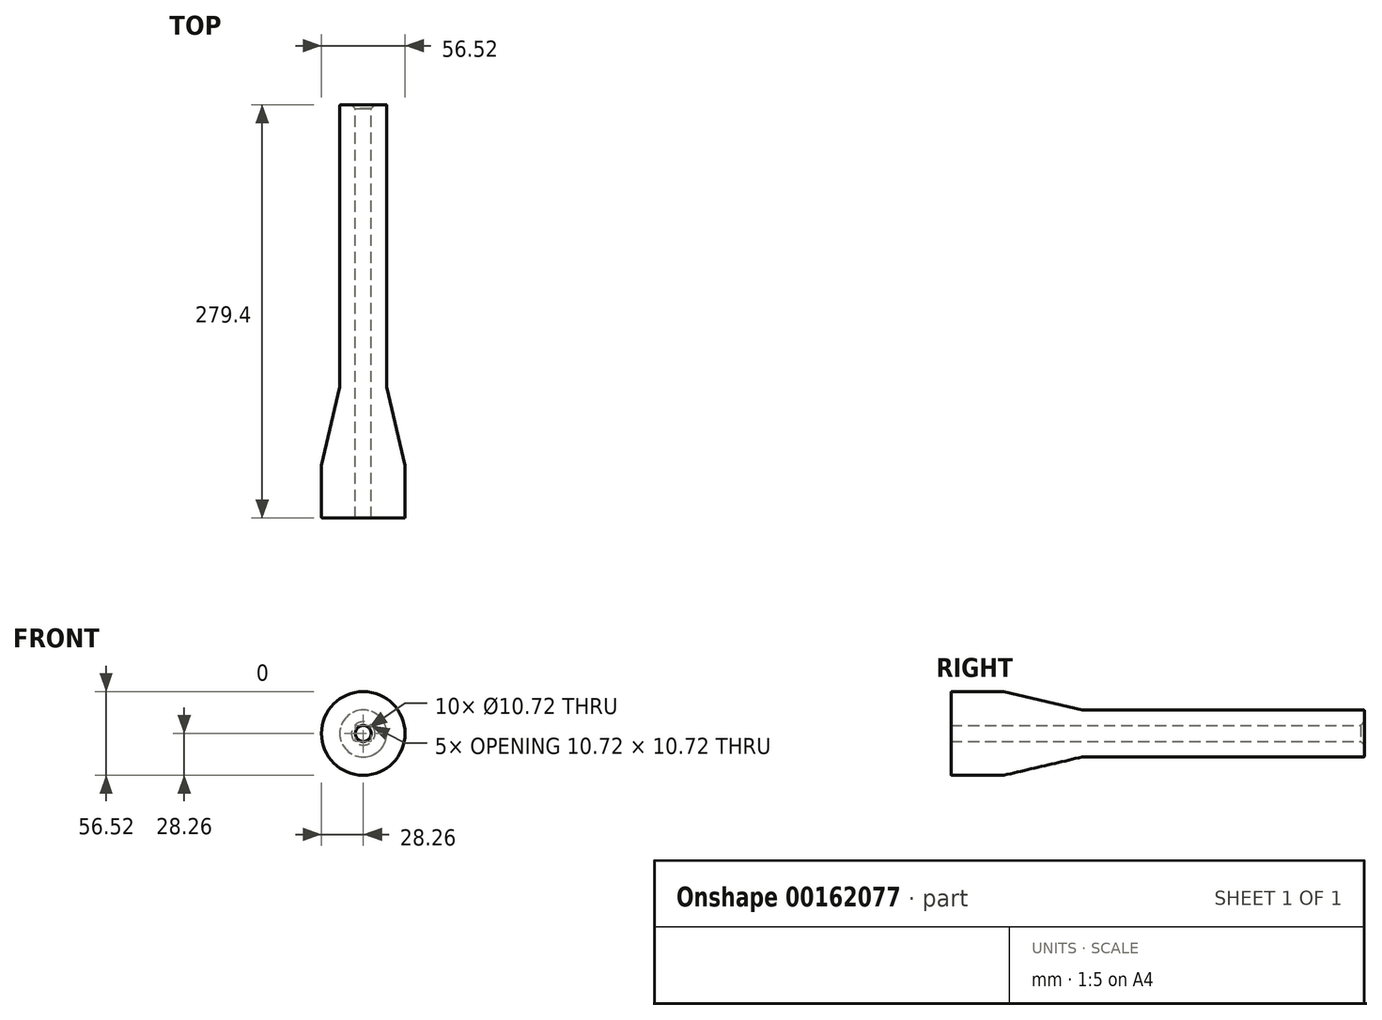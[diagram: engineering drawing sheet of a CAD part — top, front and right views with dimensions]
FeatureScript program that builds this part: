
annotation { "Feature Type Name" : "Feature", "Feature Type Description" : "" }
export const myFeature = defineFeature(function(context is Context, id is Id, definition is map)
    precondition{}
    {
        {
            var Q0;
            Q0=qCreatedBy(makeId("Right.planeOp"),FACE);
            var sketch = newSketch(context, id + "F0", { "sketchPlane" : qUnion([Q0])});
            skLineSegment(sketch, "E0", {"start": v(0, 0) * mm, "end": v(0, 28.26) * mm});
            skLineSegment(sketch, "E1", {"start": v(0, 28.26) * mm, "end": v(35.56, 28.26) * mm});
            skLineSegment(sketch, "E2", {"start": v(35.56, 28.26) * mm, "end": v(88.65, 15.87) * mm});
            skLineSegment(sketch, "E3", {"start": v(88.65, 15.87) * mm, "end": v(279.4, 15.87) * mm});
            skLineSegment(sketch, "E4", {"start": v(279.4, 15.87) * mm, "end": v(279.4, 0) * mm});
            skLineSegment(sketch, "E5", {"start": v(0, 0) * mm, "end": v(279.4, 0) * mm});
            skSolve(sketch);
        }
        {
            var Q0;
            Q0 = qSketchRegion(id + "F0", true);
            var Q1;
            Q1=sQuery(id+"F0.wireOp",EDGE,"E5");
            revolve(context, id + "F1", {"entities" : qUnion([Q0]), "axis" : qUnion([Q1]), "revolveType" : RevolveType.FULL});
        }
        {
            var Q0;
            Q0=makeQuery(id+"F1.opRevolve","SWEPT_FACE",FACE,{"disambiguationData":[OSD([sQuery(id+"F0.wireOp",EDGE,"E4")])]});
            var sketch = newSketch(context, id + "F2", { "sketchPlane" : qUnion([Q0])});
            skPoint(sketch, "E6", {"position": v(0, 0) * mm});
            skSolve(sketch);
        }
        {
            var Q0;
            Q0=sQuery(id+"F2.wireOp",VERTEX,"E6");
            var Q1;
            Q1=makeQuery(id+"F1.opRevolve","SWEPT_BODY",BODY,{"disambiguationData":[OSD([sQuery(id+"F0.wireOp",EDGE,"E0"),sQuery(id+"F0.wireOp",EDGE,"E1"),sQuery(id+"F0.wireOp",EDGE,"E2"),sQuery(id+"F0.wireOp",EDGE,"E3"),sQuery(id+"F0.wireOp",EDGE,"E4"),sQuery(id+"F0.wireOp",EDGE,"E5")])]});
            hole(context, id + "F3", {"style" : HoleStyle.C_SINK, "endStyle" : HoleEndStyle.BLIND, "holeDiameter" : 10.72 * mm, "cSinkDiameter" : 15.88 * mm, "cSinkAngle" : 90 * degree, "holeDepth" : 191 * mm, "locations" : qUnion([Q0]), "scope" : qUnion([Q1])});
        }
        {
            var Q0;
            Q0=makeQuery(id+"F1.opRevolve","SWEPT_FACE",FACE,{"disambiguationData":[OSD([sQuery(id+"F0.wireOp",EDGE,"E0")])]});
            var sketch = newSketch(context, id + "F4", { "sketchPlane" : qUnion([Q0])});
            skPoint(sketch, "E7", {"position": v(0, 0) * mm});
            skSolve(sketch);
        }
        {
            var Q0;
            Q0=sQuery(id+"F4.wireOp",VERTEX,"E7");
            var Q1;
            Q1=makeQuery(id+"F1.opRevolve","SWEPT_BODY",BODY,{"disambiguationData":[OSD([sQuery(id+"F0.wireOp",EDGE,"E0"),sQuery(id+"F0.wireOp",EDGE,"E1"),sQuery(id+"F0.wireOp",EDGE,"E2"),sQuery(id+"F0.wireOp",EDGE,"E3"),sQuery(id+"F0.wireOp",EDGE,"E4"),sQuery(id+"F0.wireOp",EDGE,"E5")])]});
            hole(context, id + "F5", {"style" : HoleStyle.SIMPLE, "endStyle" : HoleEndStyle.BLIND, "holeDiameter" : 10.72 * mm, "holeDepth" : 241.8 * mm, "locations" : qUnion([Q0]), "scope" : qUnion([Q1])});
        }
        {
            var Q0;
            Q0=makeQuery(id+"F1.opRevolve","SWEPT_EDGE",EDGE,{"disambiguationData":[OSD([sQuery(id+"F0.wireOp",EDGE,"E0"),sQuery(id+"F0.wireOp",EDGE,"E1")])]});
            var Q1;
            Q1=makeQuery(id+"F1.opRevolve","SWEPT_EDGE",EDGE,{"disambiguationData":[OSD([sQuery(id+"F0.wireOp",EDGE,"E1"),sQuery(id+"F0.wireOp",EDGE,"E2")])]});
            var Q2;
            Q2=makeQuery(id+"F1.opRevolve","SWEPT_EDGE",EDGE,{"disambiguationData":[OSD([sQuery(id+"F0.wireOp",EDGE,"E2"),sQuery(id+"F0.wireOp",EDGE,"E3")])]});
            var Q3;
            Q3=makeQuery(id+"F1.opRevolve","SWEPT_EDGE",EDGE,{"disambiguationData":[OSD([sQuery(id+"F0.wireOp",EDGE,"E3"),sQuery(id+"F0.wireOp",EDGE,"E4")])]});
            fillet(context, id + "F6", {"entities" : qUnion([Q0, Q1, Q2, Q3]), "radius" : 0.5 * mm, "tangentPropagation" : true, "allowEdgeOverflow" : false});
        }
    });
